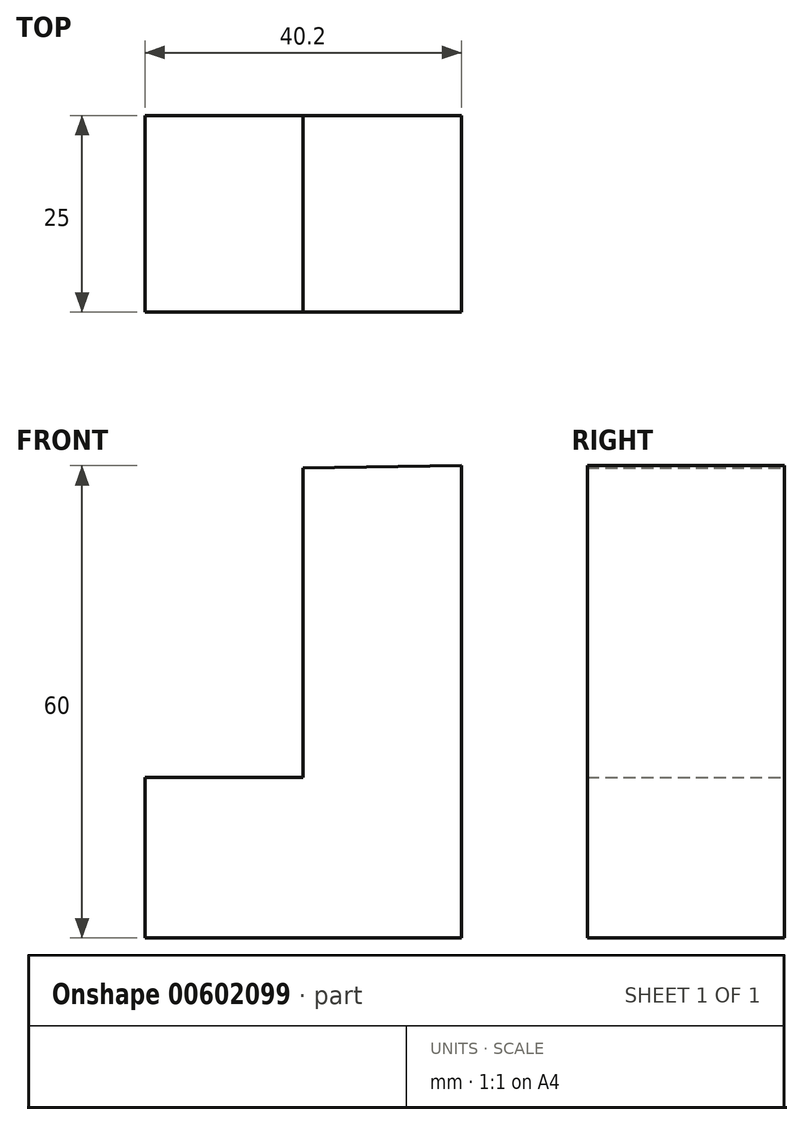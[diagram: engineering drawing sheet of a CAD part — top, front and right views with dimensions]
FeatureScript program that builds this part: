
annotation { "Feature Type Name" : "Feature", "Feature Type Description" : "" }
export const myFeature = defineFeature(function(context is Context, id is Id, definition is map)
    precondition{}
    {
        {
            var Q0;
            Q0=qCreatedBy(makeId("Front.planeOp"),FACE);
            var sketch = newSketch(context, id + "F0", { "sketchPlane" : qUnion([Q0])});
            skLineSegment(sketch, "E0", {"start": v(9.75, 32.1) * mm, "end": v(9.75, -27.9) * mm});
            skLineSegment(sketch, "E1", {"start": v(9.75, -27.9) * mm, "end": v(-30.45, -27.9) * mm});
            skLineSegment(sketch, "E2", {"start": v(-30.45, -27.9) * mm, "end": v(-30.45, -7.5) * mm});
            skLineSegment(sketch, "E3", {"start": v(-30.45, -7.5) * mm, "end": v(-10.35, -7.5) * mm});
            skLineSegment(sketch, "E4", {"start": v(-10.35, -7.5) * mm, "end": v(-10.35, 31.8) * mm});
            skLineSegment(sketch, "E5", {"start": v(-10.35, 31.8) * mm, "end": v(9.75, 32.1) * mm});
            skSolve(sketch);
        }
        {
            var Q0;
            Q0=makeQuery(id+"F0.imprint","IMPRINT",FACE,{"disambiguationData":[TD([[makeQuery(id+"F0.imprint","IMPRINT",EDGE,{"derivedFrom":sQuery(id+"F0.wireOp",EDGE,"E0")}),-1.0]])]});
            extrude(context, id + "F1", {"entities" : qUnion([Q0]), "depth" : 25 * mm, "offsetDistance" : 25 * mm});
        }
    });
